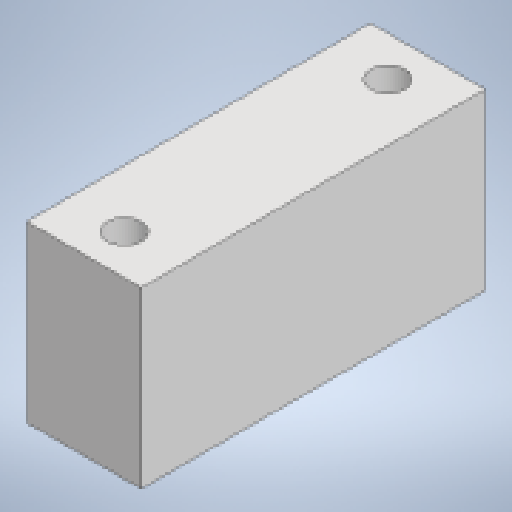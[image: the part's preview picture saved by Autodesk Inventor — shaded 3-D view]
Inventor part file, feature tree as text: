
AUTODESK INVENTOR PART (.ipt)
format: ipt  version: 2023 (Build 270158000, 158)  size: 123,392 bytes
history: native  units: mm
features: extrude x2, sketch x2, projected_geometry x1
ambient origin geometry x8: Origin, YZ Plane, XZ Plane, XY Plane, X Axis, Y Axis, Z Axis, Center Point
bodies: Solid1 (feature_tree)
feature tree (5):
  extrude  "Extrusion1"  Depth=20.0mm
  extrude  "Extrusion2"  Depth=30.4mm
  sketch  "Sketch1"  dims[d0=60.0mm d1=20.0mm]
  sketch  "Sketch2"  dims[d2=6.0mm d3=6.0mm d4=46.0mm d5=30.4mm d6=0.0mm d7=2.917mm d8=0.0mm]
  projected_geometry  "Projected Loop1"
